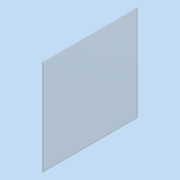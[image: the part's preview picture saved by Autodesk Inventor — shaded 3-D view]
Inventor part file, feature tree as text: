
AUTODESK INVENTOR PART (.ipt)
format: ipt  version: 2016 (Build 200138000, 138)  size: 82,432 bytes
history: native  units: mm
features: extrude x1, sketch x1
ambient origin geometry x8: Origin, YZ Plane, XZ Plane, XY Plane, X Axis, Y Axis, Z Axis, Center Point
bodies: Solid1 (feature_tree)
feature tree (2):
  extrude  "Extrusion1"  Depth=360.0mm
  sketch  "Sketch1"  dims[d0=360.0mm d1=360.0mm d2=3.0mm d3=0.0mm]
